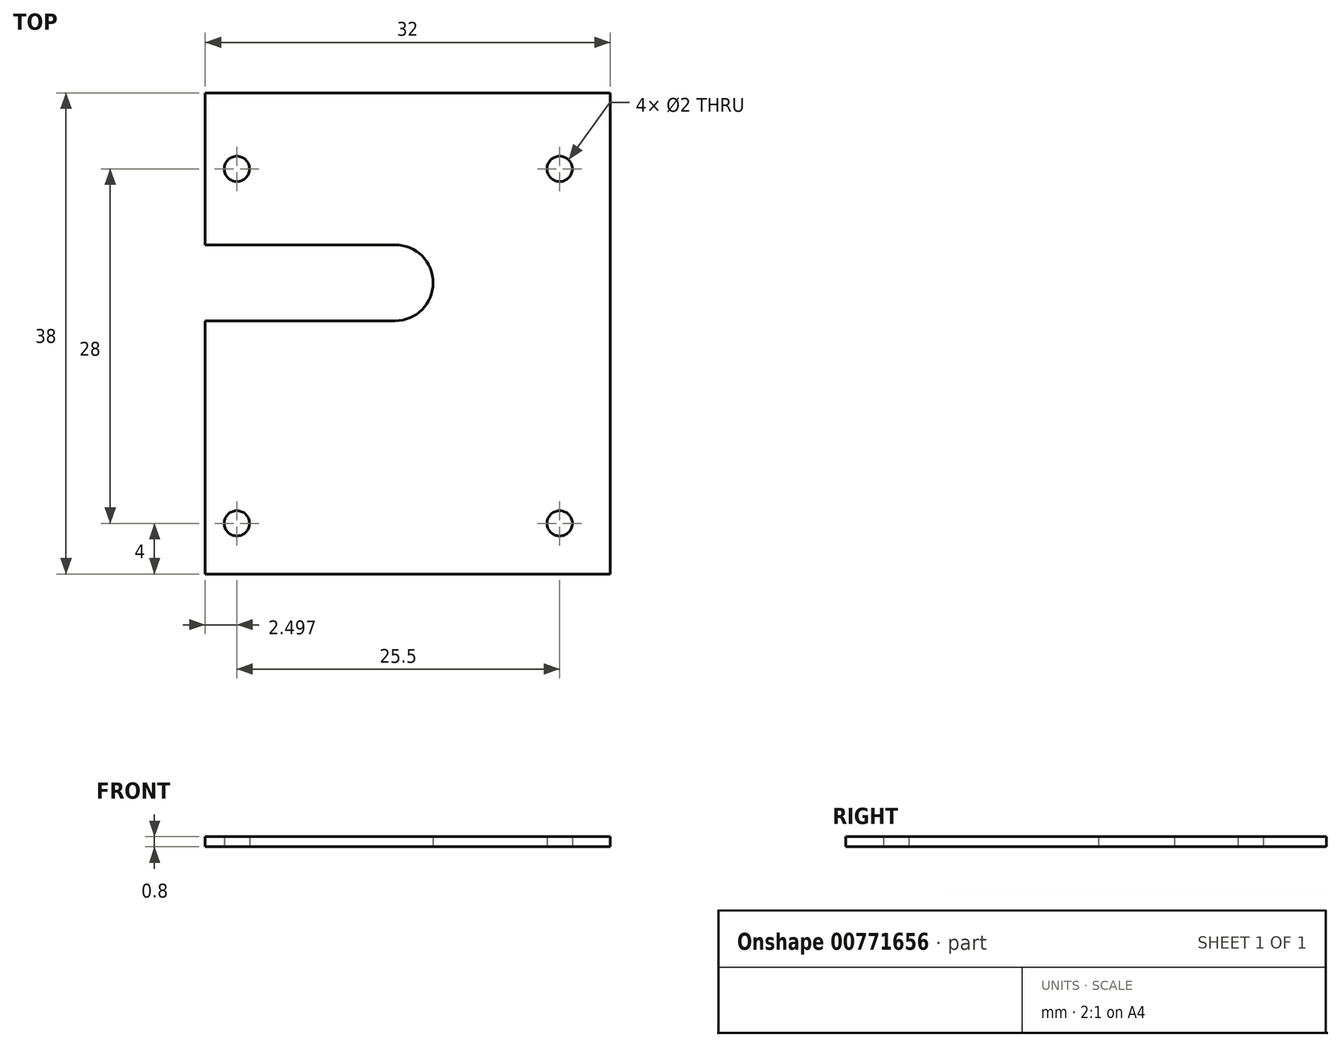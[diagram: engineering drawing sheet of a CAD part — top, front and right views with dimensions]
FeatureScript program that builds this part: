
annotation { "Feature Type Name" : "Feature", "Feature Type Description" : "" }
export const myFeature = defineFeature(function(context is Context, id is Id, definition is map)
    precondition{}
    {
        {
            var Q0;
            Q0=qCreatedBy(makeId("Top.planeOp"),FACE);
            var sketch = newSketch(context, id + "F0", { "sketchPlane" : qUnion([Q0])});
            skLineSegment(sketch, "E0.bottom", {"start": v(-25.96, 20.27) * mm, "end": v(6.04, 20.27) * mm});
            skLineSegment(sketch, "E0.top", {"start": v(-25.96, -17.73) * mm, "end": v(6.04, -17.73) * mm});
            skLineSegment(sketch, "E0.left", {"start": v(-25.96, 20.27) * mm, "end": v(-25.96, -17.73) * mm});
            skLineSegment(sketch, "E0.right", {"start": v(6.04, 20.27) * mm, "end": v(6.04, -17.73) * mm});
            skSolve(sketch);
        }
        {
            var Q0;
            Q0 = qSketchRegion(id + "F0", true);
            extrude(context, id + "F1", {"entities" : qUnion([Q0]), "depth" : 0.8 * mm, "offsetDistance" : 25 * mm});
        }
        {
            var Q0;
            Q0=makeQuery(id+"F1.opExtrude","CAP_FACE",FACE,{"disambiguationData":[OSD([sQuery(id+"F0.wireOp",EDGE,"E0.bottom"),sQuery(id+"F0.wireOp",EDGE,"E0.top"),sQuery(id+"F0.wireOp",EDGE,"E0.left"),sQuery(id+"F0.wireOp",EDGE,"E0.right")])],"isStart":true});
            var sketch = newSketch(context, id + "F2", { "sketchPlane" : qUnion([Q0])});
            skCircle(sketch, "E1", {"center": v(-23.46, 13.73) * mm, "radius": 1 * mm});
            skCircle(sketch, "E2", {"center": v(-23.46, -14.27) * mm, "radius": 1 * mm});
            skCircle(sketch, "E3", {"center": v(2.04, 13.73) * mm, "radius": 1 * mm});
            skCircle(sketch, "E4", {"center": v(2.04, -14.27) * mm, "radius": 1 * mm});
            skLineSegment(sketch, "E5.bottom", {"start": v(-25.96, -2.27) * mm, "end": v(-7.96, -2.27) * mm});
            skLineSegment(sketch, "E5.top", {"start": v(-25.96, -8.27) * mm, "end": v(-7.96, -8.27) * mm});
            skLineSegment(sketch, "E5.left", {"start": v(-25.96, -2.27) * mm, "end": v(-25.96, -8.27) * mm});
            skLineSegment(sketch, "E5.right", {"start": v(-7.96, -2.27) * mm, "end": v(-7.96, -8.27) * mm});
            skSolve(sketch);
        }
        {
            var Q0;
            Q0 = qSketchRegion(id + "F2", true);
            extrude(context, id + "F3", {"entities" : qUnion([Q0]), "operationType" : NewBodyOperationType.REMOVE, "endBound" : BoundingType.UP_TO_NEXT, "oppositeDirection" : true, "depth" : 25 * mm, "offsetDistance" : 25 * mm});
        }
        {
            var Q0;
            Q0=makeQuery(id+"F3.boolean.opBoolean","COPY",EDGE,{"derivedFrom":makeQuery(id+"F3.opExtrude","SWEPT_EDGE",EDGE,{"disambiguationData":[OSD([sQuery(id+"F2.wireOp",EDGE,"E5.top"),sQuery(id+"F2.wireOp",EDGE,"E5.right")])]})});
            var Q1;
            Q1=makeQuery(id+"F3.boolean.opBoolean","COPY",EDGE,{"derivedFrom":makeQuery(id+"F3.opExtrude","SWEPT_EDGE",EDGE,{"disambiguationData":[OSD([sQuery(id+"F2.wireOp",EDGE,"E5.bottom"),sQuery(id+"F2.wireOp",EDGE,"E5.right")])]})});
            fillet(context, id + "F4", {"entities" : qUnion([Q0, Q1]), "radius" : 3 * mm, "tangentPropagation" : true, "allowEdgeOverflow" : false});
        }
    });
